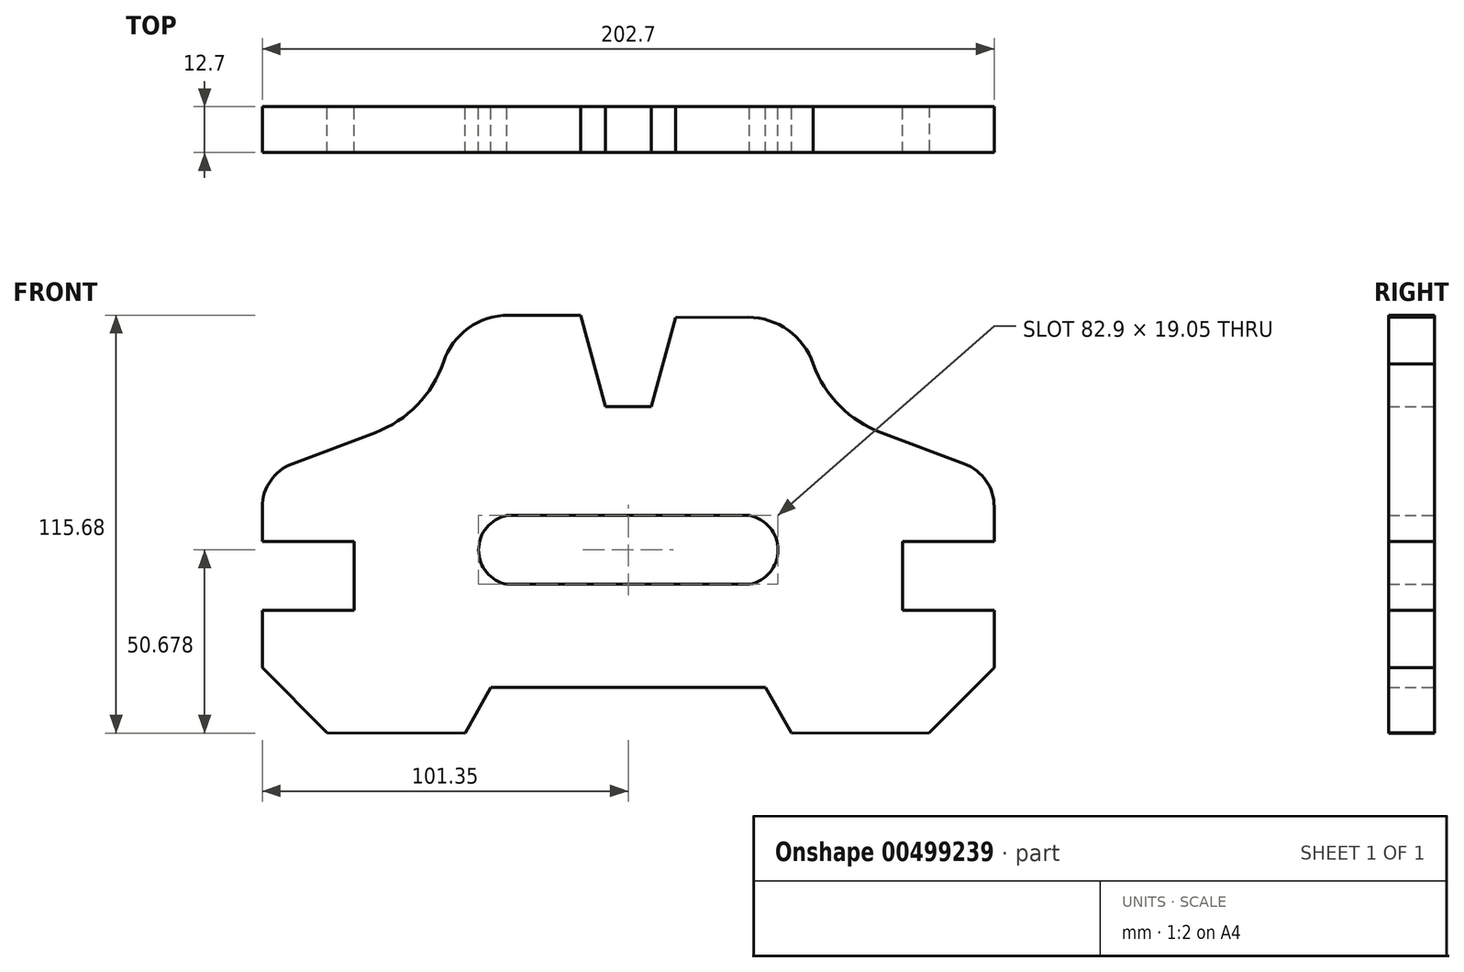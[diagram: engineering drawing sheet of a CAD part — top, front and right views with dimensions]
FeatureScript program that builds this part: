
annotation { "Feature Type Name" : "Feature", "Feature Type Description" : "" }
export const myFeature = defineFeature(function(context is Context, id is Id, definition is map)
    precondition{}
    {
        {
            var Q0;
            Q0=qCreatedBy(makeId("Front.planeOp"),FACE);
            var sketch = newSketch(context, id + "F0", { "sketchPlane" : qUnion([Q0])});
            skPoint(sketch, "E0.middle", {"position": v(0, 0) * mm});
            skArc(sketch, "E1", {"start": v(-33.6, -3.47) * mm, "mid": v(-41.45, -13) * mm, "end": v(-33.6, -22.52) * mm});
            skLineSegment(sketch, "E2", {"start": v(-6.35, 26.73) * mm, "end": v(-13.12, 52) * mm});
            skLineSegment(sketch, "E3", {"start": v(-6.35, 26.73) * mm, "end": v(-6.35, 52) * mm, "construction": true});
            skLineSegment(sketch, "E4", {"start": v(-13.12, 52) * mm, "end": v(-33.15, 52) * mm});
            skLineSegment(sketch, "E5", {"start": v(-101.35, -10.7) * mm, "end": v(-101.35, -1.05) * mm});
            skArc(sketch, "E6", {"start": v(-101.35, -1.05) * mm, "mid": v(-99.09, 6.17) * mm, "end": v(-93.12, 10.83) * mm});
            skArc(sketch, "E7", {"start": v(-33.15, 52) * mm, "mid": v(-44.26, 48.43) * mm, "end": v(-51.2, 39.05) * mm});
            skLineSegment(sketch, "E8", {"start": v(-38.05, -51.1) * mm, "end": v(-45.22, -63.67) * mm});
            skLineSegment(sketch, "E9", {"start": v(-101.35, -10.7) * mm, "end": v(-75.95, -10.7) * mm});
            skLineSegment(sketch, "E10", {"start": v(-75.95, -29.76) * mm, "end": v(-101.35, -29.76) * mm});
            skLineSegment(sketch, "E11", {"start": v(-101.35, -29.76) * mm, "end": v(-101.35, -63.54) * mm});
            skLineSegment(sketch, "E12", {"start": v(-45.22, -63.67) * mm, "end": v(-45.26, -82.62) * mm, "construction": true});
            skLineSegment(sketch, "E13", {"start": v(-45.22, -63.67) * mm, "end": v(-61.66, -92) * mm, "construction": true});
            skLineSegment(sketch, "E14", {"start": v(-75.95, -10.7) * mm, "end": v(-75.95, -29.76) * mm});
            skLineSegment(sketch, "E15.MirrorCS", {"start": v(6.35, 26.73) * mm, "end": v(13.12, 51.37) * mm});
            skArc(sketch, "E16.MirrorCS", {"start": v(101.35, -1.05) * mm, "mid": v(99.09, 6.17) * mm, "end": v(93.12, 10.83) * mm});
            skLineSegment(sketch, "E17.MirrorCS", {"start": v(101.35, -10.7) * mm, "end": v(101.35, -1.05) * mm});
            skArc(sketch, "E18.MirrorCS", {"start": v(33.6, -3.47) * mm, "mid": v(41.45, -13) * mm, "end": v(33.6, -22.52) * mm});
            skLineSegment(sketch, "E19.MirrorCS", {"start": v(101.35, -10.7) * mm, "end": v(75.95, -10.7) * mm});
            skLineSegment(sketch, "E20.MirrorCS", {"start": v(75.95, -10.7) * mm, "end": v(75.95, -29.76) * mm});
            skLineSegment(sketch, "E21.MirrorCS", {"start": v(75.95, -29.76) * mm, "end": v(101.35, -29.76) * mm});
            skLineSegment(sketch, "E22.MirrorCS", {"start": v(101.35, -29.76) * mm, "end": v(101.35, -63.54) * mm});
            skLineSegment(sketch, "E23.MirrorCS", {"start": v(38.05, -51.1) * mm, "end": v(45.21, -63.67) * mm});
            skLineSegment(sketch, "E24", {"start": v(-38.05, -51.1) * mm, "end": v(38.05, -51.1) * mm});
            skLineSegment(sketch, "E25", {"start": v(-33.6, -22.52) * mm, "end": v(33.6, -22.52) * mm});
            skLineSegment(sketch, "E26", {"start": v(-33.6, -3.47) * mm, "end": v(33.6, -3.47) * mm});
            skLineSegment(sketch, "E27", {"start": v(-6.35, 26.73) * mm, "end": v(6.35, 26.73) * mm});
            skLineSegment(sketch, "E28", {"start": v(-93.12, 10.83) * mm, "end": v(-70.1, 19.5) * mm});
            skLineSegment(sketch, "E29.MirrorCS", {"start": v(93.12, 10.83) * mm, "end": v(70.1, 19.5) * mm});
            skArc(sketch, "E30", {"start": v(-51.2, 39.05) * mm, "mid": v(-58.45, 27.14) * mm, "end": v(-70.1, 19.5) * mm});
            skArc(sketch, "E31.MirrorCS", {"start": v(51.2, 38.46) * mm, "mid": v(58.55, 26.89) * mm, "end": v(70.1, 19.5) * mm});
            skArc(sketch, "E32.MirrorCS", {"start": v(33.15, 51.42) * mm, "mid": v(44.26, 47.84) * mm, "end": v(51.2, 38.46) * mm});
            skLineSegment(sketch, "E33", {"start": v(13.12, 51.37) * mm, "end": v(33.15, 51.42) * mm});
            skLineSegment(sketch, "E34", {"start": v(45.21, -63.67) * mm, "end": v(101.35, -63.54) * mm});
            skLineSegment(sketch, "E35", {"start": v(-45.22, -63.67) * mm, "end": v(-101.35, -63.54) * mm});
            skSolve(sketch);
        }
        {
            var Q0;
            Q0=makeQuery(id+"F0.imprint","IMPRINT",FACE,{"disambiguationData":[TD([[makeQuery(id+"F0.imprint","IMPRINT",EDGE,{"derivedFrom":sQuery(id+"F0.wireOp",EDGE,"E1")}),-1.0]])]});
            extrude(context, id + "F1", {"entities" : qUnion([Q0]), "endBound" : BoundingType.SYMMETRIC, "depth" : 12.7 * mm, "offsetDistance" : 25.4 * mm});
        }
        {
            var Q0;
            Q0=makeQuery(id+"F1.opExtrude","SWEPT_EDGE",EDGE,{"disambiguationData":[OSD([sQuery(id+"F0.wireOp",EDGE,"E11"),sQuery(id+"F0.wireOp",EDGE,"E35")])]});
            var Q1;
            Q1=makeQuery(id+"F1.opExtrude","SWEPT_EDGE",EDGE,{"disambiguationData":[OSD([sQuery(id+"F0.wireOp",EDGE,"E22.MirrorCS"),sQuery(id+"F0.wireOp",EDGE,"E34")])]});
            chamfer(context, id + "F2", {"entities" : qUnion([Q0, Q1]), "width" : 18.03 * mm, "tangentPropagation" : true});
        }
    });
